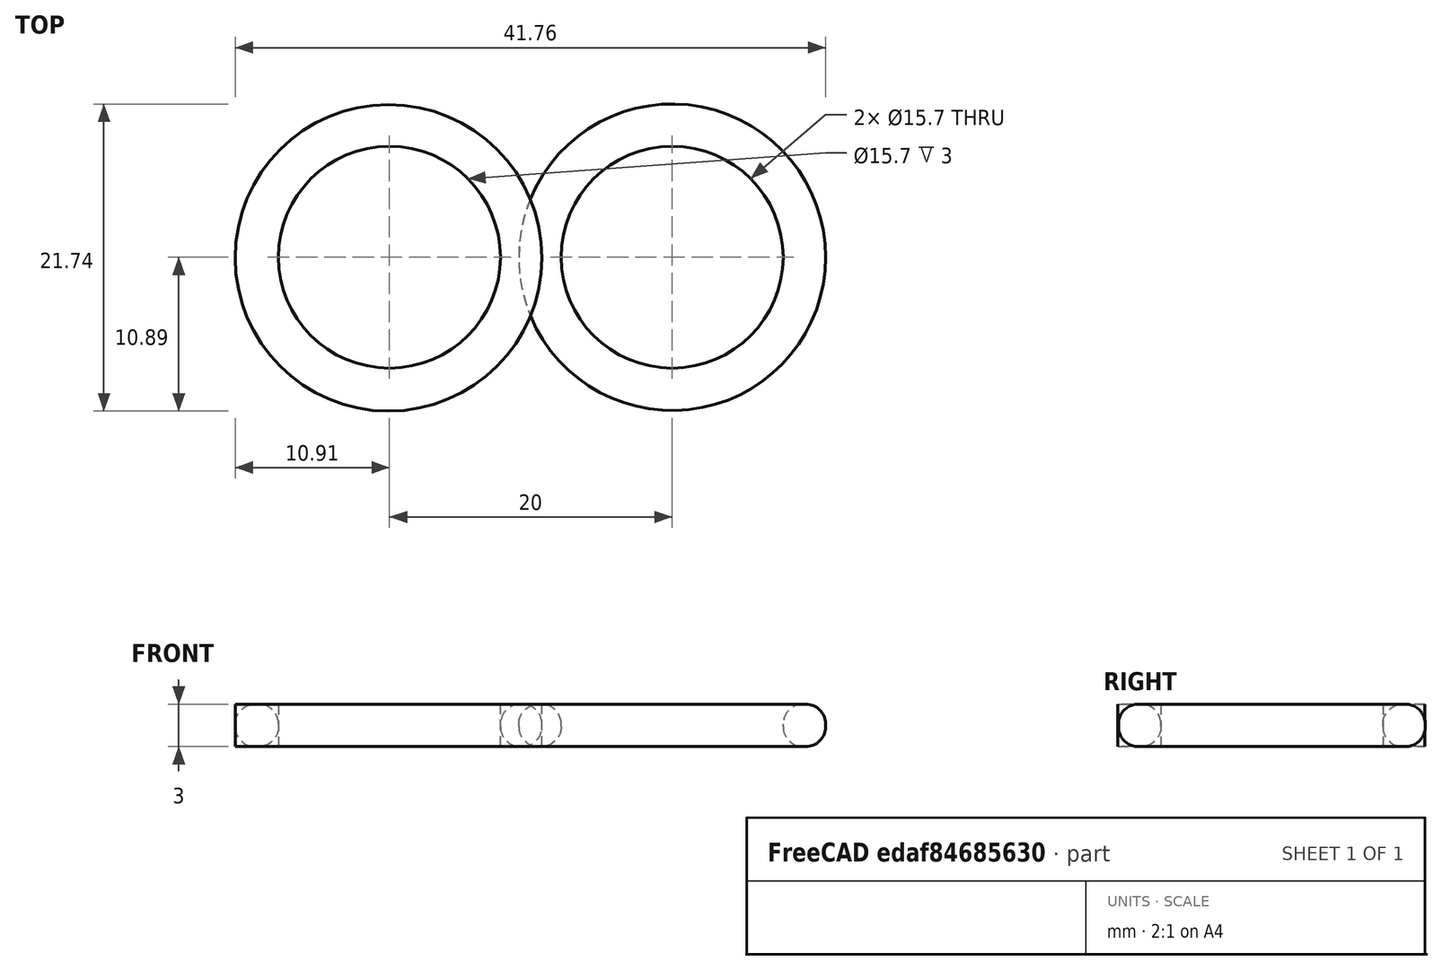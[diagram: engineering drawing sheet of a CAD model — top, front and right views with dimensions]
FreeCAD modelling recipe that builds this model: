
FCSTD DOCUMENT  (FreeCAD 0.18R16117 (Git))
Label: Ring
License: All rights reserved
LicenseURL: http://en.wikipedia.org/wiki/All_rights_reserved
objects: Part::Cylinder×2, Part::Fillet×2, Part::Cut×1, Sketcher::SketchObject×1, PartDesign::Pad×1, PartDesign::Body×1
note: 9 computed .brp shape members not serialized (recipe doc carries the construction recipe); baked Part::Feature solids carry a one-line shape summary decoded from their .brp

FEATURE [Part::Cylinder] Cylinder
  Angle = 360
  AttacherType = Attacher::AttachEngine3D
  Height = 10
  Placement = pos=(7,0,0) rot=(0,0,1;0rad)
  Radius = 7.85
FEATURE [Part::Cylinder] Cylinder001
  Angle = 360
  AttacherType = Attacher::AttachEngine3D
  Height = 3
  Placement = pos=(7,0,0) rot=(0,0,1;0rad)
  Radius = 10.85
FEATURE [Part::Cut] Cut
  Base = -> Cylinder001
  Tool = -> Cylinder
FEATURE [Part::Fillet] Fillet
  Base = -> Cut
  Edges = 4 edges r=1.4: [Edge1,Edge3,Edge4,Edge5]
  Placement = pos=(13,0,0) rot=(0,0,1;0rad)
FEATURE [Sketcher::SketchObject] Sketch
  MapMode = 5
  Support = -> [XY_Plane]
  sketch-geometry (2):
    g0: Circle CenterX=0 CenterY=0 CenterZ=0 NormalX=0 NormalY=0 NormalZ=1 AngleXU=0 Radius=7.85
    g1: Circle CenterX=-0.063757 CenterY=-0.042504 CenterZ=0 NormalX=0 NormalY=0 NormalZ=1 AngleXU=0 Radius=10.85
  constraints (2):
    c: Radius(g0) = 7.85
    c: Radius(g1) = 10.85
FEATURE [PartDesign::Pad] Pad
  Length = 3
  Length2 = 100
  Profile = -> Sketch
  Type = 0
FEATURE [PartDesign::Body] Body
  Group = -> [Sketch,Pad]
  Origin = -> Origin
  Tip = -> Pad
FEATURE [Part::Fillet] Fillet001
  Base = -> Pad
  Edges = 4 edges r=1.4: [Edge2,Edge3,Edge5,Edge6]
